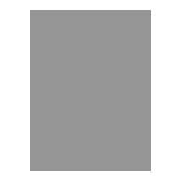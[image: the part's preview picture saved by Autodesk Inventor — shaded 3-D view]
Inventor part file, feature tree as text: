
AUTODESK INVENTOR PART (.ipt)
format: ipt  version: 2019.4 (Build 234330000, 330)  size: 114,688 bytes
history: native  units: mm (DEFAULTED — no unit token found)
features: other x4, plane x4, split x3, sketch x2
ambient origin geometry x8: Origin, YZ Plane, XZ Plane, XY Plane, X Axis, Y Axis, Z Axis, Center Point
bodies: Solid1 (feature_tree), Body (feature_tree)
feature tree (13):
  parser-record x1  (decoder bookkeeping rows leaked as tree rows — omitted from the tree; the rows remain in map.json)
  other  "Driven Length"
  other  "Start plane"
  other  "End plane"
  plane  "Work Plane6"
  split  "Split3"
  plane  "Work Plane7"
  split  "Split4"
  plane  "Work Plane8"
  split  "Split5"
  sketch  "Sketch3"  dims[d0=12.7mm]
  plane  "Work Plane3"
  sketch  "Sketch4"  dims[d1=12.7mm d2=602.702861mm d3=0.0mm d4=6.35mm d5=6.35mm d6=-6.35mm d7=596.352861mm d8=90.0deg d9=602.702861mm]
